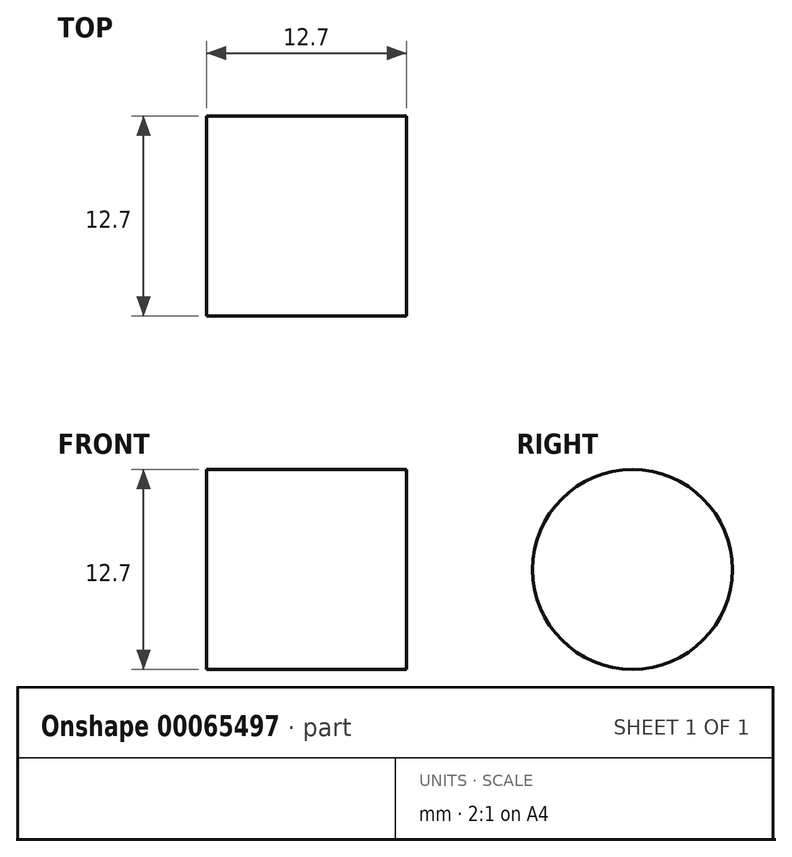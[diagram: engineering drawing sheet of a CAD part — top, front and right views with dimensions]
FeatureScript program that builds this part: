
annotation { "Feature Type Name" : "Feature", "Feature Type Description" : "" }
export const myFeature = defineFeature(function(context is Context, id is Id, definition is map)
    precondition{}
    {
        {
            var Q0;
            Q0=qCreatedBy(makeId("Top.planeOp"),FACE);
            var sketch = newSketch(context, id + "F0", { "sketchPlane" : qUnion([Q0])});
            skLineSegment(sketch, "E0", {"start": v(0, 0) * mm, "end": v(0, 12.7) * mm});
            skLineSegment(sketch, "E1", {"start": v(0, 12.7) * mm, "end": v(12.7, 12.7) * mm});
            skLineSegment(sketch, "E2", {"start": v(12.7, 12.7) * mm, "end": v(12.7, 0) * mm});
            skLineSegment(sketch, "E3", {"start": v(12.7, 6.35) * mm, "end": v(0, 6.35) * mm});
            skSolve(sketch);
        }
        {
            var Q0;
            {var subQ0=sQuery(id+"F0.wireOp",EDGE,"E1");Q0=makeQuery(id+"F0.imprint","IMPRINT",FACE,{"disambiguationData":[TD([[makeQuery(id+"F0.imprint","IMPRINT",EDGE,{"derivedFrom":subQ0}),-1.0]])]});}
            var Q1;
            Q1=sQuery(id+"F0.wireOp",EDGE,"E3");
            revolve(context, id + "F1", {"entities" : qUnion([Q0]), "axis" : qUnion([Q1]), "revolveType" : RevolveType.FULL});
        }
        {
            var Q0;
            Q0=makeQuery(id+"F1.opRevolve","SWEPT_FACE",FACE,{"disambiguationData":[OSD([sQuery(id+"F0.wireOp",EDGE,"E0")])]});
            var sketch = newSketch(context, id + "F2", { "sketchPlane" : qUnion([Q0])});
            skCircle(sketch, "E4", {"center": v(-6.35, 0) * mm, "radius": 2.55 * mm});
            skSolve(sketch);
        }
        {
            var Q0;
            Q0 = qSketchRegion(id + "F2", true);
            extrude(context, id + "F3", {"entities" : qUnion([Q0]), "operationType" : NewBodyOperationType.ADD, "oppositeDirection" : true, "depth" : 9.52 * mm});
        }
    });
